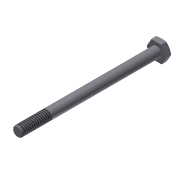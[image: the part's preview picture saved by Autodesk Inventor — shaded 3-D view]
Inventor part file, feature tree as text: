
AUTODESK INVENTOR PART (.ipt)
format: ipt  version: 2013 (Build 170138000, 138)  size: 156,672 bytes
history: native  units: in
note: dims shown in document units (in); Inventor stores cm internally (conversion verified against a paired STEP export)
features: sketch x3, extrude x2, projected_geometry x2, thread x1, chamfer x1, revolve x1, fillet x1
ambient origin geometry x8: Origin, YZ Plane, XZ Plane, XY Plane, X Axis, Y Axis, Z Axis, Center Point
bodies: Solid1 (feature_tree)
feature tree (11):
  extrude  "Extrusion1"  Depth=3.5in TaperAngle=0.0deg
  extrude  "Extrusion2"  Depth=0.1562in TaperAngle=0.0deg
  thread  "Thread1"  [1 undecoded]
  chamfer  "Chamfer1"  Distance=0.02in Angle=45.0deg
  revolve  "Revolution1"  [1 undecoded]
  fillet  "Fillet1"  [1 undecoded]
  sketch  "Sketch1"  dims[d0=0.25in d1=3.5in d2=0.0in]
  sketch  "Sketch2"  dims[d3=0.4375in d4=0.1562in d5=0.0in d6=0.75in d7=0.0in d8=0.02in d9=0.125in d10=45.0deg]
  sketch  "Sketch3"  dims[d11=90.0deg d12=0.01in]
  projected_geometry  "Projected Loop1"
  projected_geometry  "Projected Loop2"
note: 3 required parameter values undecoded (feature->parameter linkage not recoverable at this tier; creation-order binding heuristic only, values carry confidence <= 0.55)